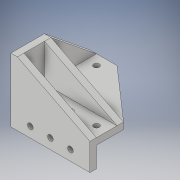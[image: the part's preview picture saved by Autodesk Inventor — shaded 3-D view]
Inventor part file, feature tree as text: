
AUTODESK INVENTOR PART (.ipt)
format: ipt  version: 2019 (Build 230136000, 136)  size: 199,680 bytes
history: native  units: in
note: dims shown in document units (in); Inventor stores cm internally (conversion verified against a paired STEP export)
features: extrude x7, sketch x7, projected_geometry x2, plane x1
ambient origin geometry x8: Origin, YZ Plane, XZ Plane, XY Plane, X Axis, Y Axis, Z Axis, Center Point
bodies: Solid1 (feature_tree)
feature tree (17):
  extrude  "Extrusion1"  Depth=0.7874in
  extrude  "Extrusion2"  Depth=0.25in
  extrude  "Extrusion3"  Depth=2.4528in TaperAngle=0.0deg
  plane  "Work Plane1"
  extrude  "Extrusion4"  Depth=0.7874in
  extrude  "Extrusion5"  Depth=0.3937in
  extrude  "Extrusion7"  Depth=0.3937in
  extrude  "Extrusion8"  Depth=0.25in
  sketch  "Sketch1"  dims[d0=2.0in d1=0.7874in]
  sketch  "Sketch2"  dims[d2=0.7874in d3=0.25in]
  sketch  "Sketch3"  dims[d4=0.25in d5=2.4528in d6=0.0in]
  sketch  "Sketch4"  dims[d7=0.7874in d8=0.2165in]
  projected_geometry  "Projected Loop1"
  sketch  "Sketch5"  dims[d9=0.75in d10=1.1811in d12=0.7687in d13=0.3937in d15=1.0in]
  sketch  "Sketch7"  dims[d17=2.4528in d18=0.0in d19=0.3937in]
  sketch  "Sketch8"  dims[d20=0.2165in d21=0.75in d22=1.1811in d24=0.7687in d25=0.3937in d27=1.0in d29=2.4528in d30=0.0in d31=-0.7874in d32=0.7874in d33=1.1811in d35=1.0in d36=0.3937in d38=1.0in d40=0.2165in d41=1.1811in d43=1.0in d44=0.3937in d46=1.0in d48=0.25in d49=0.0in d50=0.25in d51=0.25in d52=0.25in d53=0.0in d59=0.25in d60=0.0in d61=0.25in d62=0.0in]
  projected_geometry  "Projected Loop2"
